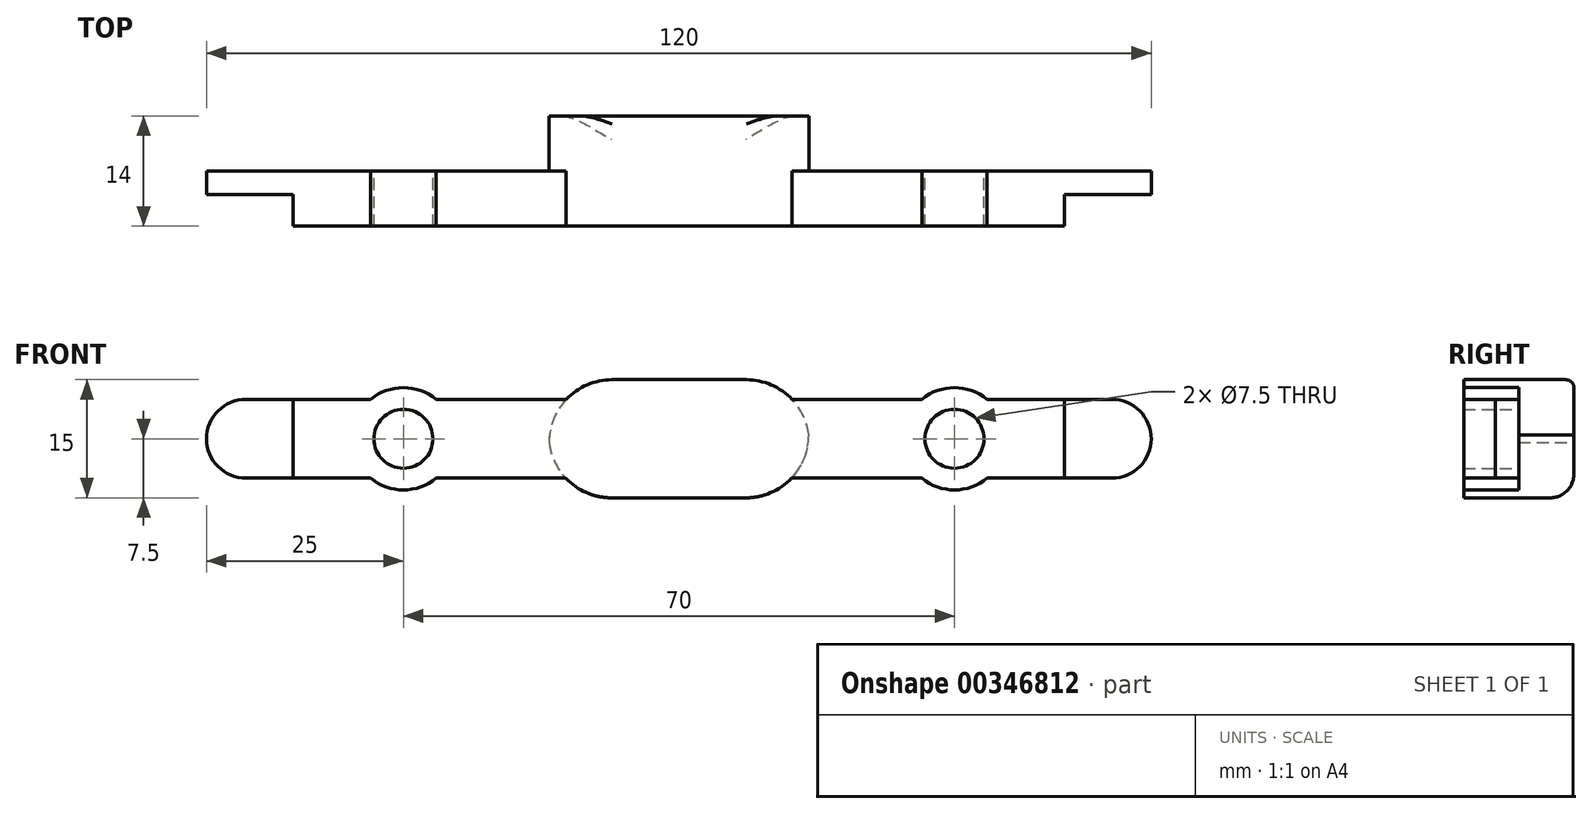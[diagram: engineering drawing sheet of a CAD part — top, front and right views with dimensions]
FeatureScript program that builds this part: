
annotation { "Feature Type Name" : "Feature", "Feature Type Description" : "" }
export const myFeature = defineFeature(function(context is Context, id is Id, definition is map)
    precondition{}
    {
        {
            var Q0;
            Q0=qCreatedBy(makeId("Front.planeOp"),FACE);
            var sketch = newSketch(context, id + "F0", { "sketchPlane" : qUnion([Q0])});
            skLineSegment(sketch, "E0.bottom", {"start": v(-60, -5) * mm, "end": v(60, -5) * mm});
            skLineSegment(sketch, "E0.top", {"start": v(-60, -15) * mm, "end": v(60, -15) * mm});
            skLineSegment(sketch, "E0.left", {"start": v(-60, -5) * mm, "end": v(-60, -15) * mm});
            skLineSegment(sketch, "E0.right", {"start": v(60, -5) * mm, "end": v(60, -15) * mm});
            skSolve(sketch);
        }
        {
            var Q0;
            Q0=qCreatedBy(makeId("Front.planeOp"),FACE);
            var sketch = newSketch(context, id + "F1", { "sketchPlane" : qUnion([Q0])});
            skCircle(sketch, "E1", {"center": v(-35, -10) * mm, "radius": 6.5 * mm});
            skSolve(sketch);
        }
        {
            var Q0;
            Q0 = qSketchRegion(id + "F0", true);
            extrude(context, id + "F2", {"entities" : qUnion([Q0]), "depth" : 7 * mm});
        }
        {
            var Q0;
            Q0 = qSketchRegion(id + "F1", true);
            extrude(context, id + "F3", {"entities" : qUnion([Q0]), "operationType" : NewBodyOperationType.ADD, "depth" : 7 * mm});
        }
        {
            var Q0;
            Q0=qCreatedBy(makeId("Front.planeOp"),FACE);
            var sketch = newSketch(context, id + "F4", { "sketchPlane" : qUnion([Q0])});
            skCircle(sketch, "E2", {"center": v(-35, -10) * mm, "radius": 3.75 * mm});
            skSolve(sketch);
        }
        {
            var Q0;
            Q0 = qSketchRegion(id + "F4", true);
            extrude(context, id + "F5", {"entities" : qUnion([Q0]), "operationType" : NewBodyOperationType.REMOVE, "depth" : 7 * mm});
        }
        {
            var Q0;
            Q0=qCreatedBy(makeId("Front.planeOp"),FACE);
            var sketch = newSketch(context, id + "F6", { "sketchPlane" : qUnion([Q0])});
            skLineSegment(sketch, "E3.bottom", {"start": v(-16.5, -2.5) * mm, "end": v(16.5, -2.5) * mm});
            skLineSegment(sketch, "E3.top", {"start": v(-16.5, -17.5) * mm, "end": v(16.5, -17.5) * mm});
            skLineSegment(sketch, "E3.left", {"start": v(-16.5, -2.5) * mm, "end": v(-16.5, -17.5) * mm});
            skLineSegment(sketch, "E3.right", {"start": v(16.5, -2.5) * mm, "end": v(16.5, -17.5) * mm});
            skSolve(sketch);
        }
        {
            var Q0;
            Q0=makeQuery(id+"F6.imprint","IMPRINT",FACE,{"disambiguationData":[TD([[makeQuery(id+"F6.imprint","IMPRINT",EDGE,{"derivedFrom":sQuery(id+"F6.wireOp",EDGE,"E3.bottom")}),-1.0]])]});
            var Q1;
            Q1 = qSketchRegion(id + "F6", true);
            extrude(context, id + "F7", {"entities" : qUnion([Q0, Q1]), "operationType" : NewBodyOperationType.ADD, "depth" : 7 * mm});
        }
        {
            var Q0;
            Q0 = qSketchRegion(id + "F6", true);
            extrude(context, id + "F8", {"entities" : qUnion([Q0]), "operationType" : NewBodyOperationType.ADD, "oppositeDirection" : true, "depth" : 7 * mm});
        }
        {
            var Q0;
            {var subQ0=sQuery(id+"F6.wireOp",EDGE,"E3.left");var subQ1=sQuery(id+"F6.wireOp",EDGE,"E3.bottom");Q0=makeQuery(id+"F8.boolean.opBoolean","MERGE",EDGE,{"derivedFrom":[makeQuery(id+"F7.opExtrude","SWEPT_EDGE",EDGE,{"disambiguationData":[OSD([subQ1,subQ0])]}),makeQuery(id+"F8.opExtrude","SWEPT_EDGE",EDGE,{"disambiguationData":[OSD([subQ1,subQ0])]})]});}
            fillet(context, id + "F9", {"entities" : qUnion([Q0]), "radius" : 8 * mm, "tangentPropagation" : true, "allowEdgeOverflow" : false});
        }
        {
            var Q0;
            {var subQ0=sQuery(id+"F6.wireOp",EDGE,"E3.left");var subQ1=sQuery(id+"F6.wireOp",EDGE,"E3.top");Q0=makeQuery(id+"F8.boolean.opBoolean","MERGE",EDGE,{"derivedFrom":[makeQuery(id+"F7.opExtrude","SWEPT_EDGE",EDGE,{"disambiguationData":[OSD([subQ1,subQ0])]}),makeQuery(id+"F8.opExtrude","SWEPT_EDGE",EDGE,{"disambiguationData":[OSD([subQ1,subQ0])]})]});}
            fillet(context, id + "F10", {"entities" : qUnion([Q0]), "radius" : 8 * mm, "tangentPropagation" : true, "allowEdgeOverflow" : false});
        }
        {
            var Q0;
            {var subQ0=sQuery(id+"F6.wireOp",EDGE,"E3.right");var subQ1=sQuery(id+"F6.wireOp",EDGE,"E3.top");Q0=makeQuery(id+"F8.boolean.opBoolean","MERGE",EDGE,{"derivedFrom":[makeQuery(id+"F7.opExtrude","SWEPT_EDGE",EDGE,{"disambiguationData":[OSD([subQ1,subQ0])]}),makeQuery(id+"F8.opExtrude","SWEPT_EDGE",EDGE,{"disambiguationData":[OSD([subQ1,subQ0])]})]});}
            fillet(context, id + "F11", {"entities" : qUnion([Q0]), "radius" : 8 * mm, "tangentPropagation" : true, "allowEdgeOverflow" : false});
        }
        {
            var Q0;
            {var subQ0=sQuery(id+"F6.wireOp",EDGE,"E3.right");var subQ1=sQuery(id+"F6.wireOp",EDGE,"E3.bottom");Q0=makeQuery(id+"F8.boolean.opBoolean","MERGE",EDGE,{"derivedFrom":[makeQuery(id+"F7.opExtrude","SWEPT_EDGE",EDGE,{"disambiguationData":[OSD([subQ1,subQ0])]}),makeQuery(id+"F8.opExtrude","SWEPT_EDGE",EDGE,{"disambiguationData":[OSD([subQ1,subQ0])]})]});}
            fillet(context, id + "F12", {"entities" : qUnion([Q0]), "radius" : 8 * mm, "tangentPropagation" : true, "allowEdgeOverflow" : false});
        }
        {
            var Q0;
            Q0=qCreatedBy(makeId("Top.planeOp"),FACE);
            var sketch = newSketch(context, id + "F13", { "sketchPlane" : qUnion([Q0])});
            skLineSegment(sketch, "E4.bottom", {"start": v(49, -3) * mm, "end": v(60, -3) * mm});
            skLineSegment(sketch, "E4.top", {"start": v(49, -7) * mm, "end": v(60, -7) * mm});
            skLineSegment(sketch, "E4.left", {"start": v(49, -3) * mm, "end": v(49, -7) * mm});
            skLineSegment(sketch, "E4.right", {"start": v(60, -3) * mm, "end": v(60, -7) * mm});
            skSolve(sketch);
        }
        {
            var Q0;
            Q0 = qSketchRegion(id + "F13", true);
            extrude(context, id + "F14", {"entities" : qUnion([Q0]), "operationType" : NewBodyOperationType.REMOVE, "oppositeDirection" : true, "depth" : 17 * mm});
        }
        {
            var Q0;
            Q0=makeQuery(id+"F2.opExtrude","SWEPT_EDGE",EDGE,{"disambiguationData":[OSD([sQuery(id+"F0.wireOp",EDGE,"E0.top"),sQuery(id+"F0.wireOp",EDGE,"E0.right")])]});
            fillet(context, id + "F15", {"entities" : qUnion([Q0]), "radius" : 5 * mm, "tangentPropagation" : true, "allowEdgeOverflow" : false});
        }
        {
            var Q0;
            Q0=makeQuery(id+"F2.opExtrude","SWEPT_EDGE",EDGE,{"disambiguationData":[OSD([sQuery(id+"F0.wireOp",EDGE,"E0.bottom"),sQuery(id+"F0.wireOp",EDGE,"E0.right")])]});
            fillet(context, id + "F16", {"entities" : qUnion([Q0]), "radius" : 5 * mm, "tangentPropagation" : true, "allowEdgeOverflow" : false});
        }
        {
            var Q0;
            Q0=makeQuery(id+"F8.opExtrude","CAP_EDGE",EDGE,{"disambiguationData":[OSD([sQuery(id+"F6.wireOp",EDGE,"E3.top")])],"isStart":false});
            fillet(context, id + "F17", {"entities" : qUnion([Q0]), "radius" : 3 * mm, "allowEdgeOverflow" : false});
        }
        {
            var Q0;
            Q0=makeQuery(id+"F8.opExtrude","CAP_EDGE",EDGE,{"disambiguationData":[OSD([sQuery(id+"F6.wireOp",EDGE,"E3.bottom")])],"isStart":false});
            fillet(context, id + "F18", {"entities" : qUnion([Q0]), "radius" : 1 * mm, "allowEdgeOverflow" : false});
        }
        {
            var Q0;
            Q0=qCreatedBy(makeId("Front.planeOp"),FACE);
            var sketch = newSketch(context, id + "F19", { "sketchPlane" : qUnion([Q0])});
            skCircle(sketch, "E5", {"center": v(35, -10) * mm, "radius": 6.5 * mm});
            skSolve(sketch);
        }
        {
            var Q0;
            Q0=qCreatedBy(makeId("Front.planeOp"),FACE);
            var sketch = newSketch(context, id + "F20", { "sketchPlane" : qUnion([Q0])});
            skCircle(sketch, "E6", {"center": v(35, -10) * mm, "radius": 3.75 * mm});
            skSolve(sketch);
        }
        {
            var Q0;
            Q0 = qSketchRegion(id + "F19", true);
            extrude(context, id + "F21", {"entities" : qUnion([Q0]), "operationType" : NewBodyOperationType.ADD, "depth" : 7 * mm});
        }
        {
            var Q0;
            Q0 = qSketchRegion(id + "F20", true);
            extrude(context, id + "F22", {"entities" : qUnion([Q0]), "operationType" : NewBodyOperationType.REMOVE, "depth" : 7 * mm});
        }
        {
            var Q0;
            Q0=qCreatedBy(makeId("Top.planeOp"),FACE);
            var sketch = newSketch(context, id + "F23", { "sketchPlane" : qUnion([Q0])});
            skLineSegment(sketch, "E7.bottom", {"start": v(-60, -3) * mm, "end": v(-49, -3) * mm});
            skLineSegment(sketch, "E7.top", {"start": v(-60, -7) * mm, "end": v(-49, -7) * mm});
            skLineSegment(sketch, "E7.left", {"start": v(-60, -3) * mm, "end": v(-60, -7) * mm});
            skLineSegment(sketch, "E7.right", {"start": v(-49, -3) * mm, "end": v(-49, -7) * mm});
            skSolve(sketch);
        }
        {
            var Q0;
            Q0 = qSketchRegion(id + "F23", true);
            extrude(context, id + "F24", {"entities" : qUnion([Q0]), "operationType" : NewBodyOperationType.REMOVE, "oppositeDirection" : true, "depth" : 17 * mm});
        }
        {
            var Q0;
            Q0=makeQuery(id+"F2.opExtrude","SWEPT_EDGE",EDGE,{"disambiguationData":[OSD([sQuery(id+"F0.wireOp",EDGE,"E0.top"),sQuery(id+"F0.wireOp",EDGE,"E0.left")])]});
            fillet(context, id + "F25", {"entities" : qUnion([Q0]), "radius" : 5 * mm, "tangentPropagation" : true, "allowEdgeOverflow" : false});
        }
        {
            var Q0;
            Q0=makeQuery(id+"F2.opExtrude","SWEPT_EDGE",EDGE,{"disambiguationData":[OSD([sQuery(id+"F0.wireOp",EDGE,"E0.bottom"),sQuery(id+"F0.wireOp",EDGE,"E0.left")])]});
            fillet(context, id + "F26", {"entities" : qUnion([Q0]), "radius" : 5 * mm, "tangentPropagation" : true, "allowEdgeOverflow" : false});
        }
    });
